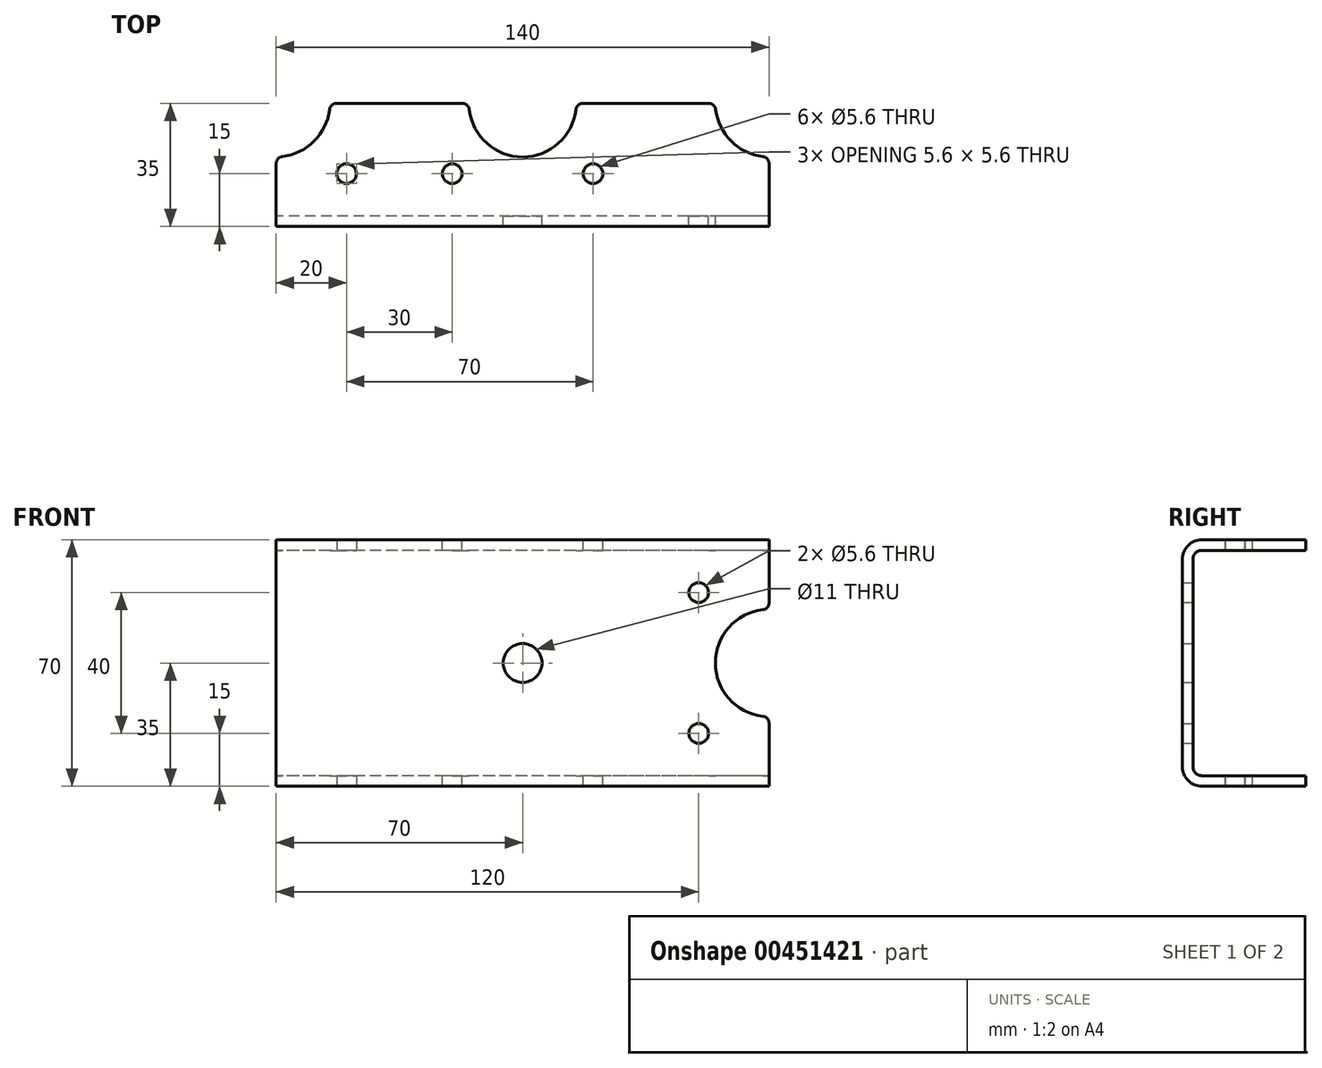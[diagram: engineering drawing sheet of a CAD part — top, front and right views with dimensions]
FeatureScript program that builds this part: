
annotation { "Feature Type Name" : "Feature", "Feature Type Description" : "" }
export const myFeature = defineFeature(function(context is Context, id is Id, definition is map)
    precondition{}
    {
        {
            var Q0;
            Q0=qCreatedBy(makeId("Front.planeOp"),FACE);
            var sketch = newSketch(context, id + "F0", { "sketchPlane" : qUnion([Q0])});
            skLineSegment(sketch, "E0.bottom", {"start": v(0, -32) * mm, "end": v(-32, -32) * mm});
            skLineSegment(sketch, "E0.top", {"start": v(0, 32) * mm, "end": v(-32, 32) * mm});
            skLineSegment(sketch, "E0.left", {"start": v(0, -32) * mm, "end": v(0, 32) * mm, "construction": true});
            skLineSegment(sketch, "E0.right", {"start": v(-32, -32) * mm, "end": v(-32, 32) * mm});
            skLineSegment(sketch, "E1.0", {"start": v(0, -35) * mm, "end": v(-35, -35) * mm});
            skLineSegment(sketch, "E1.1", {"start": v(-35, -35) * mm, "end": v(-35, 35) * mm});
            skLineSegment(sketch, "E1.2", {"start": v(0, 35) * mm, "end": v(-35, 35) * mm});
            skLineSegment(sketch, "E2", {"start": v(0, 35) * mm, "end": v(0, 32) * mm});
            skLineSegment(sketch, "E3", {"start": v(0, -32) * mm, "end": v(0, -35) * mm});
            skSolve(sketch);
        }
        {
            var Q0;
            Q0=makeQuery(id+"F0.imprint","IMPRINT",FACE,{"disambiguationData":[TD([[makeQuery(id+"F0.imprint","IMPRINT",EDGE,{"derivedFrom":sQuery(id+"F0.wireOp",EDGE,"E0.bottom")}),1.0]])]});
            extrude(context, id + "F1", {"entities" : qUnion([Q0]), "depth" : 140 * mm, "symmetric" : true});
        }
        {
            var Q0;
            Q0=makeQuery(id+"F1.opExtrude","SWEPT_EDGE",EDGE,{"disambiguationData":[OSD([sQuery(id+"F0.wireOp",EDGE,"E1.0"),sQuery(id+"F0.wireOp",EDGE,"E1.1")])]});
            var Q1;
            Q1=makeQuery(id+"F1.opExtrude","SWEPT_EDGE",EDGE,{"disambiguationData":[OSD([sQuery(id+"F0.wireOp",EDGE,"E1.1"),sQuery(id+"F0.wireOp",EDGE,"E1.2")])]});
            fillet(context, id + "F2", {"entities" : qUnion([Q0, Q1]), "radius" : 5.5 * mm, "tangentPropagation" : true, "allowEdgeOverflow" : false});
        }
        {
            var Q0;
            Q0=makeQuery(id+"F1.opExtrude","SWEPT_EDGE",EDGE,{"disambiguationData":[OSD([sQuery(id+"F0.wireOp",EDGE,"E0.top"),sQuery(id+"F0.wireOp",EDGE,"E0.right")])]});
            var Q1;
            Q1=makeQuery(id+"F1.opExtrude","SWEPT_EDGE",EDGE,{"disambiguationData":[OSD([sQuery(id+"F0.wireOp",EDGE,"E0.bottom"),sQuery(id+"F0.wireOp",EDGE,"E0.right")])]});
            fillet(context, id + "F3", {"entities" : qUnion([Q0, Q1]), "radius" : 2.5 * mm, "tangentPropagation" : true, "allowEdgeOverflow" : false});
        }
        {
            var Q0;
            Q0=qCreatedBy(makeId("Top.planeOp"),FACE);
            var sketch = newSketch(context, id + "F4", { "sketchPlane" : qUnion([Q0])});
            skCircle(sketch, "E4", {"center": v(0, -70) * mm, "radius": 15.25 * mm});
            skCircle(sketch, "E5", {"center": v(0, 70) * mm, "radius": 15.25 * mm});
            skSolve(sketch);
        }
        {
            var Q0;
            Q0=qSketchRegion(id+"F4",true);
            extrude(context, id + "F5", {"entities" : qUnion([Q0]), "operationType" : NewBodyOperationType.REMOVE, "oppositeDirection" : true, "depth" : 70 * mm, "symmetric" : true});
        }
        {
            var Q0;
            Q0=qCreatedBy(makeId("Top.planeOp"),FACE);
            var sketch = newSketch(context, id + "F6", { "sketchPlane" : qUnion([Q0])});
            skCircle(sketch, "E6", {"center": v(0, 0) * mm, "radius": 15.25 * mm});
            skSolve(sketch);
        }
        {
            var Q0;
            Q0=qSketchRegion(id+"F6",true);
            extrude(context, id + "F7", {"entities" : qUnion([Q0]), "operationType" : NewBodyOperationType.REMOVE, "depth" : 70 * mm, "symmetric" : true});
        }
        {
            var Q0;
            Q0=qCreatedBy(makeId("Top.planeOp"),FACE);
            var sketch = newSketch(context, id + "F8", { "sketchPlane" : qUnion([Q0])});
            skCircle(sketch, "E7", {"center": v(-20, 50) * mm, "radius": 2.8 * mm});
            skSolve(sketch);
        }
        {
            var Q0;
            Q0=qSketchRegion(id+"F8",true);
            extrude(context, id + "F9", {"entities" : qUnion([Q0]), "operationType" : NewBodyOperationType.REMOVE, "depth" : 70 * mm, "symmetric" : true});
        }
        {
            var Q0;
            Q0=qCreatedBy(makeId("Top.planeOp"),FACE);
            var sketch = newSketch(context, id + "F10", { "sketchPlane" : qUnion([Q0])});
            skCircle(sketch, "E8", {"center": v(-20, -20) * mm, "radius": 2.8 * mm});
            skCircle(sketch, "E9", {"center": v(-20, 20) * mm, "radius": 2.8 * mm});
            skSolve(sketch);
        }
        {
            var Q0;
            Q0=qSketchRegion(id+"F10",true);
            extrude(context, id + "F11", {"entities" : qUnion([Q0]), "operationType" : NewBodyOperationType.REMOVE, "oppositeDirection" : true, "depth" : 70 * mm, "symmetric" : true});
        }
        {
            var Q0;
            Q0=qCreatedBy(makeId("Right.planeOp"),FACE);
            var sketch = newSketch(context, id + "F12", { "sketchPlane" : qUnion([Q0])});
            skCircle(sketch, "E10", {"center": v(-70, 0) * mm, "radius": 15.25 * mm});
            skCircle(sketch, "E11", {"center": v(-50, 20) * mm, "radius": 2.8 * mm});
            skCircle(sketch, "E12", {"center": v(-50, -20) * mm, "radius": 2.8 * mm});
            skSolve(sketch);
        }
        {
            var Q0;
            Q0=qSketchRegion(id+"F12",true);
            extrude(context, id + "F13", {"entities" : qUnion([Q0]), "operationType" : NewBodyOperationType.REMOVE, "endBound" : BoundingType.THROUGH_ALL, "oppositeDirection" : true, "depth" : 25 * mm});
        }
        {
            var Q0;
            Q0=makeQuery(id+"F7.boolean.opBoolean","INTERSECT",EDGE,{"disambiguationData":[OD(0.0)],"derivedFrom":[makeQuery(id+"F1.opExtrude","SWEPT_FACE",FACE,{"disambiguationData":[OSD([sQuery(id+"F0.wireOp",EDGE,"E2")])]}),makeQuery(id+"F7.opExtrude","SWEPT_FACE",FACE,{"disambiguationData":[OSD([sQuery(id+"F6.wireOp",EDGE,"E6")])]})]});
            var Q1;
            Q1=makeQuery(id+"F7.boolean.opBoolean","INTERSECT",EDGE,{"disambiguationData":[OD(1.0)],"derivedFrom":[makeQuery(id+"F1.opExtrude","SWEPT_FACE",FACE,{"disambiguationData":[OSD([sQuery(id+"F0.wireOp",EDGE,"E2")])]}),makeQuery(id+"F7.opExtrude","SWEPT_FACE",FACE,{"disambiguationData":[OSD([sQuery(id+"F6.wireOp",EDGE,"E6")])]})]});
            var Q2;
            Q2=makeQuery(id+"F7.boolean.opBoolean","INTERSECT",EDGE,{"disambiguationData":[OD(1.0)],"derivedFrom":[makeQuery(id+"F1.opExtrude","SWEPT_FACE",FACE,{"disambiguationData":[OSD([sQuery(id+"F0.wireOp",EDGE,"E3")])]}),makeQuery(id+"F7.opExtrude","SWEPT_FACE",FACE,{"disambiguationData":[OSD([sQuery(id+"F6.wireOp",EDGE,"E6")])]})]});
            var Q3;
            Q3=makeQuery(id+"F7.boolean.opBoolean","INTERSECT",EDGE,{"disambiguationData":[OD(0.0)],"derivedFrom":[makeQuery(id+"F1.opExtrude","SWEPT_FACE",FACE,{"disambiguationData":[OSD([sQuery(id+"F0.wireOp",EDGE,"E3")])]}),makeQuery(id+"F7.opExtrude","SWEPT_FACE",FACE,{"disambiguationData":[OSD([sQuery(id+"F6.wireOp",EDGE,"E6")])]})]});
            fillet(context, id + "F14", {"entities" : qUnion([Q0, Q1, Q2, Q3]), "radius" : 2 * mm, "tangentPropagation" : true, "allowEdgeOverflow" : false});
        }
        {
            var Q0;
            Q0=makeQuery(id+"F5.boolean.opBoolean","INTERSECT",EDGE,{"disambiguationData":[OD(0.0)],"derivedFrom":[makeQuery(id+"F1.opExtrude","CAP_FACE",FACE,{"disambiguationData":[OSD([sQuery(id+"F0.wireOp",EDGE,"E0.bottom"),sQuery(id+"F0.wireOp",EDGE,"E0.top"),sQuery(id+"F0.wireOp",EDGE,"E0.right"),sQuery(id+"F0.wireOp",EDGE,"E1.0"),sQuery(id+"F0.wireOp",EDGE,"E1.1"),sQuery(id+"F0.wireOp",EDGE,"E1.2"),sQuery(id+"F0.wireOp",EDGE,"E2"),sQuery(id+"F0.wireOp",EDGE,"E3")])],"isStart":false}),makeQuery(id+"F5.opExtrude","SWEPT_FACE",FACE,{"disambiguationData":[OSD([sQuery(id+"F4.wireOp",EDGE,"E4")])]})]});
            var Q1;
            Q1=makeQuery(id+"F5.boolean.opBoolean","INTERSECT",EDGE,{"derivedFrom":[makeQuery(id+"F1.opExtrude","SWEPT_FACE",FACE,{"disambiguationData":[OSD([sQuery(id+"F0.wireOp",EDGE,"E2")])]}),makeQuery(id+"F5.opExtrude","SWEPT_FACE",FACE,{"disambiguationData":[OSD([sQuery(id+"F4.wireOp",EDGE,"E4")])]})]});
            var Q2;
            Q2=makeQuery(id+"F5.boolean.opBoolean","INTERSECT",EDGE,{"derivedFrom":[makeQuery(id+"F1.opExtrude","SWEPT_FACE",FACE,{"disambiguationData":[OSD([sQuery(id+"F0.wireOp",EDGE,"E3")])]}),makeQuery(id+"F5.opExtrude","SWEPT_FACE",FACE,{"disambiguationData":[OSD([sQuery(id+"F4.wireOp",EDGE,"E4")])]})]});
            var Q3;
            Q3=makeQuery(id+"F5.boolean.opBoolean","INTERSECT",EDGE,{"disambiguationData":[OD(1.0)],"derivedFrom":[makeQuery(id+"F1.opExtrude","CAP_FACE",FACE,{"disambiguationData":[OSD([sQuery(id+"F0.wireOp",EDGE,"E0.bottom"),sQuery(id+"F0.wireOp",EDGE,"E0.top"),sQuery(id+"F0.wireOp",EDGE,"E0.right"),sQuery(id+"F0.wireOp",EDGE,"E1.0"),sQuery(id+"F0.wireOp",EDGE,"E1.1"),sQuery(id+"F0.wireOp",EDGE,"E1.2"),sQuery(id+"F0.wireOp",EDGE,"E2"),sQuery(id+"F0.wireOp",EDGE,"E3")])],"isStart":false}),makeQuery(id+"F5.opExtrude","SWEPT_FACE",FACE,{"disambiguationData":[OSD([sQuery(id+"F4.wireOp",EDGE,"E4")])]})]});
            var Q4;
            Q4=makeQuery(id+"F13.boolean.opBoolean","INTERSECT",EDGE,{"disambiguationData":[OD(1.0)],"derivedFrom":[makeQuery(id+"F1.opExtrude","CAP_FACE",FACE,{"disambiguationData":[OSD([sQuery(id+"F0.wireOp",EDGE,"E0.bottom"),sQuery(id+"F0.wireOp",EDGE,"E0.top"),sQuery(id+"F0.wireOp",EDGE,"E0.right"),sQuery(id+"F0.wireOp",EDGE,"E1.0"),sQuery(id+"F0.wireOp",EDGE,"E1.1"),sQuery(id+"F0.wireOp",EDGE,"E1.2"),sQuery(id+"F0.wireOp",EDGE,"E2"),sQuery(id+"F0.wireOp",EDGE,"E3")])],"isStart":false}),makeQuery(id+"F13.opExtrude","SWEPT_FACE",FACE,{"disambiguationData":[OSD([sQuery(id+"F12.wireOp",EDGE,"E10")])]})]});
            var Q5;
            Q5=makeQuery(id+"F13.boolean.opBoolean","INTERSECT",EDGE,{"disambiguationData":[OD(0.0)],"derivedFrom":[makeQuery(id+"F1.opExtrude","CAP_FACE",FACE,{"disambiguationData":[OSD([sQuery(id+"F0.wireOp",EDGE,"E0.bottom"),sQuery(id+"F0.wireOp",EDGE,"E0.top"),sQuery(id+"F0.wireOp",EDGE,"E0.right"),sQuery(id+"F0.wireOp",EDGE,"E1.0"),sQuery(id+"F0.wireOp",EDGE,"E1.1"),sQuery(id+"F0.wireOp",EDGE,"E1.2"),sQuery(id+"F0.wireOp",EDGE,"E2"),sQuery(id+"F0.wireOp",EDGE,"E3")])],"isStart":false}),makeQuery(id+"F13.opExtrude","SWEPT_FACE",FACE,{"disambiguationData":[OSD([sQuery(id+"F12.wireOp",EDGE,"E10")])]})]});
            var Q6;
            Q6=makeQuery(id+"FLqxTyplpYU0jMX_1.1.F13.boolean.opBoolean","INTERSECT",EDGE,{"disambiguationData":[OD(0.0)],"derivedFrom":[makeQuery(id+"F1.opExtrude","CAP_FACE",FACE,{"disambiguationData":[OSD([sQuery(id+"F0.wireOp",EDGE,"E0.bottom"),sQuery(id+"F0.wireOp",EDGE,"E0.top"),sQuery(id+"F0.wireOp",EDGE,"E0.right"),sQuery(id+"F0.wireOp",EDGE,"E1.0"),sQuery(id+"F0.wireOp",EDGE,"E1.1"),sQuery(id+"F0.wireOp",EDGE,"E1.2"),sQuery(id+"F0.wireOp",EDGE,"E2"),sQuery(id+"F0.wireOp",EDGE,"E3")])],"isStart":true}),makeQuery(id+"FLqxTyplpYU0jMX_1.1.F13.opExtrude","SWEPT_FACE",FACE,{"disambiguationData":[OSD([sQuery(id+"F12.wireOp",EDGE,"E10")])]})]});
            var Q7;
            Q7=makeQuery(id+"F5.boolean.opBoolean","INTERSECT",EDGE,{"disambiguationData":[OD(1.0)],"derivedFrom":[makeQuery(id+"F1.opExtrude","CAP_FACE",FACE,{"disambiguationData":[OSD([sQuery(id+"F0.wireOp",EDGE,"E0.bottom"),sQuery(id+"F0.wireOp",EDGE,"E0.top"),sQuery(id+"F0.wireOp",EDGE,"E0.right"),sQuery(id+"F0.wireOp",EDGE,"E1.0"),sQuery(id+"F0.wireOp",EDGE,"E1.1"),sQuery(id+"F0.wireOp",EDGE,"E1.2"),sQuery(id+"F0.wireOp",EDGE,"E2"),sQuery(id+"F0.wireOp",EDGE,"E3")])],"isStart":true}),makeQuery(id+"F5.opExtrude","SWEPT_FACE",FACE,{"disambiguationData":[OSD([sQuery(id+"F4.wireOp",EDGE,"E5")])]})]});
            var Q8;
            Q8=makeQuery(id+"F5.boolean.opBoolean","INTERSECT",EDGE,{"derivedFrom":[makeQuery(id+"F1.opExtrude","SWEPT_FACE",FACE,{"disambiguationData":[OSD([sQuery(id+"F0.wireOp",EDGE,"E3")])]}),makeQuery(id+"F5.opExtrude","SWEPT_FACE",FACE,{"disambiguationData":[OSD([sQuery(id+"F4.wireOp",EDGE,"E5")])]})]});
            var Q9;
            Q9=makeQuery(id+"F5.boolean.opBoolean","INTERSECT",EDGE,{"disambiguationData":[OD(0.0)],"derivedFrom":[makeQuery(id+"F1.opExtrude","CAP_FACE",FACE,{"disambiguationData":[OSD([sQuery(id+"F0.wireOp",EDGE,"E0.bottom"),sQuery(id+"F0.wireOp",EDGE,"E0.top"),sQuery(id+"F0.wireOp",EDGE,"E0.right"),sQuery(id+"F0.wireOp",EDGE,"E1.0"),sQuery(id+"F0.wireOp",EDGE,"E1.1"),sQuery(id+"F0.wireOp",EDGE,"E1.2"),sQuery(id+"F0.wireOp",EDGE,"E2"),sQuery(id+"F0.wireOp",EDGE,"E3")])],"isStart":true}),makeQuery(id+"F5.opExtrude","SWEPT_FACE",FACE,{"disambiguationData":[OSD([sQuery(id+"F4.wireOp",EDGE,"E5")])]})]});
            var Q10;
            Q10=makeQuery(id+"F5.boolean.opBoolean","INTERSECT",EDGE,{"derivedFrom":[makeQuery(id+"F1.opExtrude","SWEPT_FACE",FACE,{"disambiguationData":[OSD([sQuery(id+"F0.wireOp",EDGE,"E2")])]}),makeQuery(id+"F5.opExtrude","SWEPT_FACE",FACE,{"disambiguationData":[OSD([sQuery(id+"F4.wireOp",EDGE,"E5")])]})]});
            var Q11;
            Q11=makeQuery(id+"FLqxTyplpYU0jMX_1.1.F13.boolean.opBoolean","INTERSECT",EDGE,{"disambiguationData":[OD(1.0)],"derivedFrom":[makeQuery(id+"F1.opExtrude","CAP_FACE",FACE,{"disambiguationData":[OSD([sQuery(id+"F0.wireOp",EDGE,"E0.bottom"),sQuery(id+"F0.wireOp",EDGE,"E0.top"),sQuery(id+"F0.wireOp",EDGE,"E0.right"),sQuery(id+"F0.wireOp",EDGE,"E1.0"),sQuery(id+"F0.wireOp",EDGE,"E1.1"),sQuery(id+"F0.wireOp",EDGE,"E1.2"),sQuery(id+"F0.wireOp",EDGE,"E2"),sQuery(id+"F0.wireOp",EDGE,"E3")])],"isStart":true}),makeQuery(id+"FLqxTyplpYU0jMX_1.1.F13.opExtrude","SWEPT_FACE",FACE,{"disambiguationData":[OSD([sQuery(id+"F12.wireOp",EDGE,"E10")])]})]});
            fillet(context, id + "F15", {"entities" : qUnion([Q0, Q1, Q2, Q3, Q4, Q5, Q6, Q7, Q8, Q9, Q10, Q11]), "radius" : 2 * mm, "tangentPropagation" : true, "allowEdgeOverflow" : false});
        }
        {
            var Q0;
            Q0=qCreatedBy(makeId("Right.planeOp"),FACE);
            var sketch = newSketch(context, id + "F16", { "sketchPlane" : qUnion([Q0])});
            skCircle(sketch, "E13", {"center": v(0, 0) * mm, "radius": 5.5 * mm});
            skSolve(sketch);
        }
        {
            var Q0;
            Q0=qSketchRegion(id+"F16",true);
            extrude(context, id + "F17", {"entities" : qUnion([Q0]), "operationType" : NewBodyOperationType.REMOVE, "endBound" : BoundingType.THROUGH_ALL, "oppositeDirection" : true, "depth" : 25 * mm});
        }
        {
            var Q0;
            Q0=makeQuery(id+"F1.opExtrude","SWEPT_BODY",BODY,{"disambiguationData":[OSD([sQuery(id+"F0.wireOp",EDGE,"E0.bottom"),sQuery(id+"F0.wireOp",EDGE,"E0.top"),sQuery(id+"F0.wireOp",EDGE,"E0.right"),sQuery(id+"F0.wireOp",EDGE,"E1.0"),sQuery(id+"F0.wireOp",EDGE,"E1.1"),sQuery(id+"F0.wireOp",EDGE,"E1.2"),sQuery(id+"F0.wireOp",EDGE,"E2"),sQuery(id+"F0.wireOp",EDGE,"E3")])]});
            var Q1;
            {var subQ0=sQuery(id+"F0.wireOp",EDGE,"E0.right");var subQ1=sQuery(id+"F0.wireOp",EDGE,"E0.top");Q1=makeQuery(id+"F13.boolean.opBoolean","SPLIT",EDGE,{"disambiguationData":[TD([makeQuery(id+"F3.opFillet","BLEND_FACE",FACE,{"disambiguationData":[OSD([subQ1,subQ0])]})])],"derivedFrom":makeQuery(id+"F1.opExtrude","CAP_EDGE",EDGE,{"disambiguationData":[OSD([subQ0])],"isStart":false})});}
            transform(context, id + "F18", {"entities" : qUnion([Q0]), "transformType" : TransformType.ROTATION, "transformAxis" : qUnion([Q1]), "angle" : 90 * degree, "makeCopy" : false});
        }
        {
            var Q0;
            Q0=makeQuery(id+"F1.opExtrude","SWEPT_BODY",BODY,{"disambiguationData":[OSD([sQuery(id+"F0.wireOp",EDGE,"E0.bottom"),sQuery(id+"F0.wireOp",EDGE,"E0.top"),sQuery(id+"F0.wireOp",EDGE,"E0.right"),sQuery(id+"F0.wireOp",EDGE,"E1.0"),sQuery(id+"F0.wireOp",EDGE,"E1.1"),sQuery(id+"F0.wireOp",EDGE,"E1.2"),sQuery(id+"F0.wireOp",EDGE,"E2"),sQuery(id+"F0.wireOp",EDGE,"E3")])]});
            transform(context, id + "F19", {"entities" : qUnion([Q0]), "transformType" : TransformType.TRANSLATION_3D, "dx" : 32 * mm, "dy" : 38 * mm, "dz" : 35 * mm, "makeCopy" : false});
        }
    });
